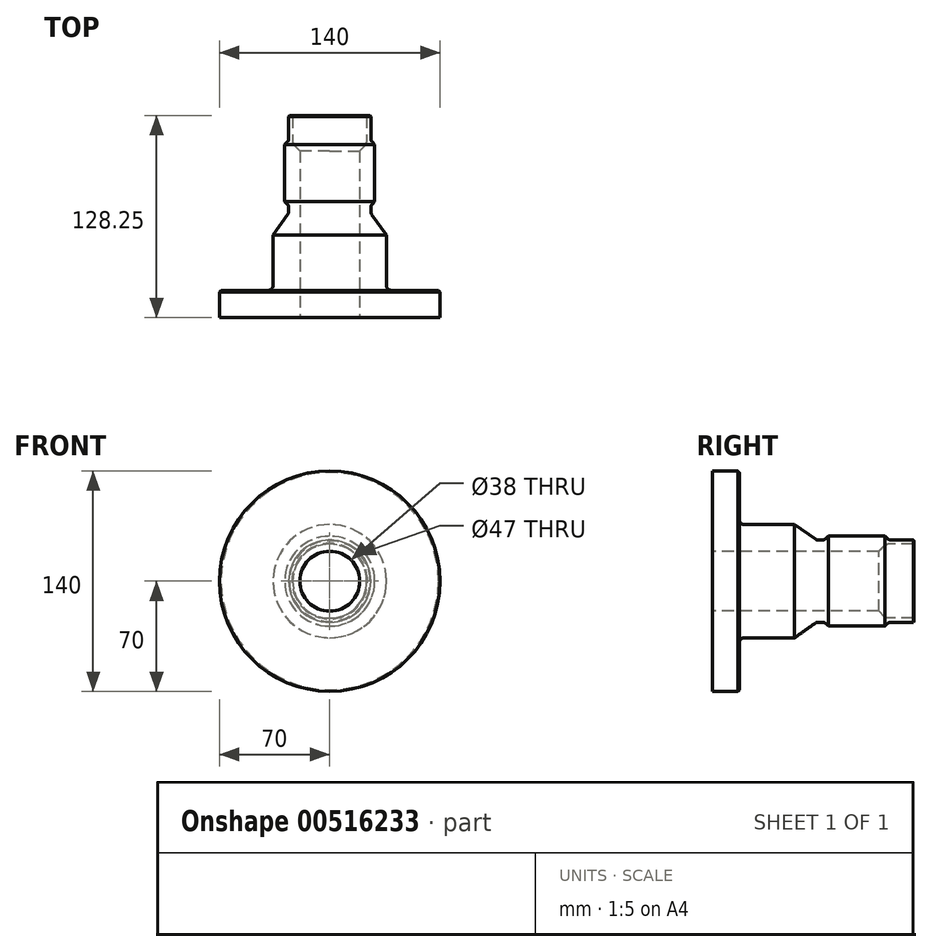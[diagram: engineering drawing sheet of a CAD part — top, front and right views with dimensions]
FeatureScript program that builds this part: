
annotation { "Feature Type Name" : "Feature", "Feature Type Description" : "" }
export const myFeature = defineFeature(function(context is Context, id is Id, definition is map)
    precondition{}
    {
        {
            var Q0;
            Q0=qCreatedBy(makeId("Right.planeOp"),FACE);
            var sketch = newSketch(context, id + "F0", { "sketchPlane" : qUnion([Q0])});
            skLineSegment(sketch, "E0", {"start": v(0, 19) * mm, "end": v(0, 70) * mm});
            skLineSegment(sketch, "E1", {"start": v(0, 70) * mm, "end": v(17.25, 70) * mm});
            skLineSegment(sketch, "E2", {"start": v(17.25, 70) * mm, "end": v(17.25, 36) * mm});
            skLineSegment(sketch, "E3", {"start": v(17.25, 36) * mm, "end": v(52.25, 36) * mm});
            skLineSegment(sketch, "E4", {"start": v(52.25, 36) * mm, "end": v(66.25, 26.12) * mm});
            skLineSegment(sketch, "E5", {"start": v(66.25, 26.12) * mm, "end": v(71.25, 26.12) * mm});
            skLineSegment(sketch, "E6", {"start": v(71.25, 26.12) * mm, "end": v(73.7, 28.58) * mm});
            skLineSegment(sketch, "E7", {"start": v(73.7, 28.57) * mm, "end": v(109.8, 28.57) * mm});
            skLineSegment(sketch, "E8", {"start": v(109.8, 28.57) * mm, "end": v(112.25, 26.12) * mm});
            skLineSegment(sketch, "E9", {"start": v(112.25, 26.12) * mm, "end": v(128.25, 26.12) * mm});
            skLineSegment(sketch, "E10", {"start": v(128.25, 26.12) * mm, "end": v(128.25, 23.5) * mm});
            skLineSegment(sketch, "E11", {"start": v(128.25, 23.5) * mm, "end": v(110.25, 23.5) * mm});
            skLineSegment(sketch, "E12", {"start": v(105.75, 19) * mm, "end": v(0, 19) * mm});
            skLineSegment(sketch, "E13", {"start": v(0, 0) * mm, "end": v(74.13, 0) * mm});
            skLineSegment(sketch, "E14", {"start": v(110.25, 23.5) * mm, "end": v(105.75, 19) * mm});
            skPoint(sketch, "E15.orphan", {"position": v(109.8, 19) * mm});
            skSolve(sketch);
        }
        {
            var Q0;
            Q0=makeQuery(id+"F0.imprint","IMPRINT",FACE,{"disambiguationData":[TD([[makeQuery(id+"F0.imprint","IMPRINT",EDGE,{"derivedFrom":sQuery(id+"F0.wireOp",EDGE,"E0")}),-1.0]])]});
            var Q1;
            Q1=sQuery(id+"F0.wireOp",EDGE,"E13");
            revolve(context, id + "F1", {"entities" : qUnion([Q0]), "axis" : qUnion([Q1]), "revolveType" : RevolveType.FULL});
        }
        {
            var Q0;
            Q0=makeQuery(id+"F1.opRevolve","SWEPT_EDGE",EDGE,{"disambiguationData":[OSD([sQuery(id+"F0.wireOp",EDGE,"E2"),sQuery(id+"F0.wireOp",EDGE,"E3")])]});
            var Q1;
            Q1=makeQuery(id+"F1.opRevolve","SWEPT_EDGE",EDGE,{"disambiguationData":[OSD([sQuery(id+"F0.wireOp",EDGE,"E4"),sQuery(id+"F0.wireOp",EDGE,"E5")])]});
            var Q2;
            Q2=makeQuery(id+"F1.opRevolve","SWEPT_EDGE",EDGE,{"disambiguationData":[OSD([sQuery(id+"F0.wireOp",EDGE,"E5"),sQuery(id+"F0.wireOp",EDGE,"E6")])]});
            var Q3;
            Q3=makeQuery(id+"F1.opRevolve","SWEPT_EDGE",EDGE,{"disambiguationData":[OSD([sQuery(id+"F0.wireOp",EDGE,"E8"),sQuery(id+"F0.wireOp",EDGE,"E9")])]});
            fillet(context, id + "F2", {"entities" : qUnion([Q0, Q1, Q2, Q3]), "radius" : 3 * mm, "tangentPropagation" : true, "allowEdgeOverflow" : false});
        }
        {
            var Q0;
            Q0=makeQuery(id+"F1.opRevolve","SWEPT_EDGE",EDGE,{"disambiguationData":[OSD([sQuery(id+"F0.wireOp",EDGE,"E11"),sQuery(id+"F0.wireOp",EDGE,"E14")])]});
            fillet(context, id + "F3", {"entities" : qUnion([Q0]), "radius" : 3 * mm, "tangentPropagation" : true, "allowEdgeOverflow" : false});
        }
        {
            var Q0;
            Q0=makeQuery(id+"F1.opRevolve","SWEPT_EDGE",EDGE,{"disambiguationData":[OSD([sQuery(id+"F0.wireOp",EDGE,"E1"),sQuery(id+"F0.wireOp",EDGE,"E2")])]});
            chamfer(context, id + "F4", {"entities" : qUnion([Q0]), "width" : 1 * mm, "tangentPropagation" : true});
        }
        {
            var Q0;
            Q0=makeQuery(id+"F1.opRevolve","SWEPT_EDGE",EDGE,{"disambiguationData":[OSD([sQuery(id+"F0.wireOp",EDGE,"E9"),sQuery(id+"F0.wireOp",EDGE,"E10")])]});
            var Q1;
            Q1=makeQuery(id+"F1.opRevolve","SWEPT_EDGE",EDGE,{"disambiguationData":[OSD([sQuery(id+"F0.wireOp",EDGE,"E10"),sQuery(id+"F0.wireOp",EDGE,"E11")])]});
            chamfer(context, id + "F5", {"entities" : qUnion([Q0, Q1]), "width" : 0.5 * mm, "tangentPropagation" : true});
        }
    });
